# Revit family: Electronics_Desono_Biamp_Two-Way-High-Coaxial-Surface-Mount-Loudspeaker_EX-S10
name_source: partatom
category: Communication Devices
units: mm (PartAtom-declared; Revit-internal decimal feet)

## family parameters
Cut with Voids When Loaded = No
Host = Face
Maintain Annotation Orientation = No
OmniClass Number = 23.85.10.11.14.14.14
Part Type = Normal
Room Calculation Point = No
Round Connector Dimension = Use Diameter
Shared = No

## types (4) — shared parameters
Compliance = ETL listed to comply with UL 1480A;CSA STD C22.2# 62368-1; EN54-24, ISO 7240-24, IEC 62368-1
Connector Description = Terminal block; 40V 200W 8Ω Nominal Impedance, 70/100V operation
Controls = Wattage / low impedance selector switch
Crossover / Protection = 1.48 kHz crossover, driver protection circuitry
Default Elevation = 1219 mm
Depth = 312 mm
Description = Desono™ EX-S10 Two-Way Coaxial 10 Surface Mount Loudspeaker
Environmental Rating = IP54 per IEC 60529, IEC 60068-2-5 (Solar Radiation),IEC 60068-2-11 (Salt Mist), IEC 60068-2-42 (SO2),IEC 60068-2-60 (Chlorine)
Finish = Refer to the Technical Drawings (pages 3-4)
Height = 529 mm
Input Connection = Lever-actuated wire clamping 4-position terminal block with pass-through
Manufacturer = Biamp
Mounting Provisions = ClickMount pan-tilt bracket or ClickMount U-Bracket
Nominal Beamwidth (H x V) = 100° x 100°
Nominal Continuous Power Handling = 49 V  (300 W, 8 Ω Nominal Impedance)
Nominal Maximum SPL = Peak - 124dB; Continuous - 118dB
Operating Environment = Indoor/Outdoor
Operating Mode = Passive with selectable low-impedance or 70 V/100 V operation
Operating Range (-10dB) = 48 Hz to 20 kHz
Product Documentation Link = https://downloads.biamp.com
Product Page URL = https://www.biamp.com
Product data url = https://bimobject.com
Rated Continuous Voltage = 45.7 V (33 dBV)
Rated Maximum SPL = Peak - 126dB, Continuous - 114dB
Recommended Amplifers = 300 W - 600 W, 8 Ω (49 V - 69 V)
Required Accessory = 48 Hz, 18 dB / oct. Butterworth high pass flter; DSP preset
Sensitivity = 1 m; 91 dB (2.83 V); 91 dB (1 W, 8 Ω)
Transducers = LF 1 x 10 (250 mm) treated paper cone;HF 1 x 1.4 (35 mm) voice coil compression driver
Transformer = 70 V: 120 W, 60 W, 30 W, 15 W;  100 V: 120 W, 60 W, 30 W
URL = https://www.biamp.com
Weight = 15.20 kgf
Width = 310 mm

## per-type parameters (varying)
| type | Bracket Material | CMX-LG | EXUB | Grill Material | Housing Material |
| EX-S10-CM W | Biamp - Plastic - White | Yes | No | Biamp - Plastic - White(Grid) | Biamp - Plastic - White |
| EX-S10-CM B | Biamp - Plastic - Black | Yes | No | Biamp - Plastic - Black(Grid) | Biamp - Plastic - Black |
| EX-S10-UB B | Biamp - Plastic - Black | No | Yes | Biamp - Plastic - Black(Grid) | Biamp - Plastic - Black |
| EX-S10-UB W | Biamp - Plastic - White | No | Yes | Biamp - Plastic - White(Grid) | Biamp - Plastic - White |

note: column(s) folded — value = type name in every type: Model

## geometry (parser evidence)
native form markers: Sweep x14
no freeform markers — native parametric forms only
